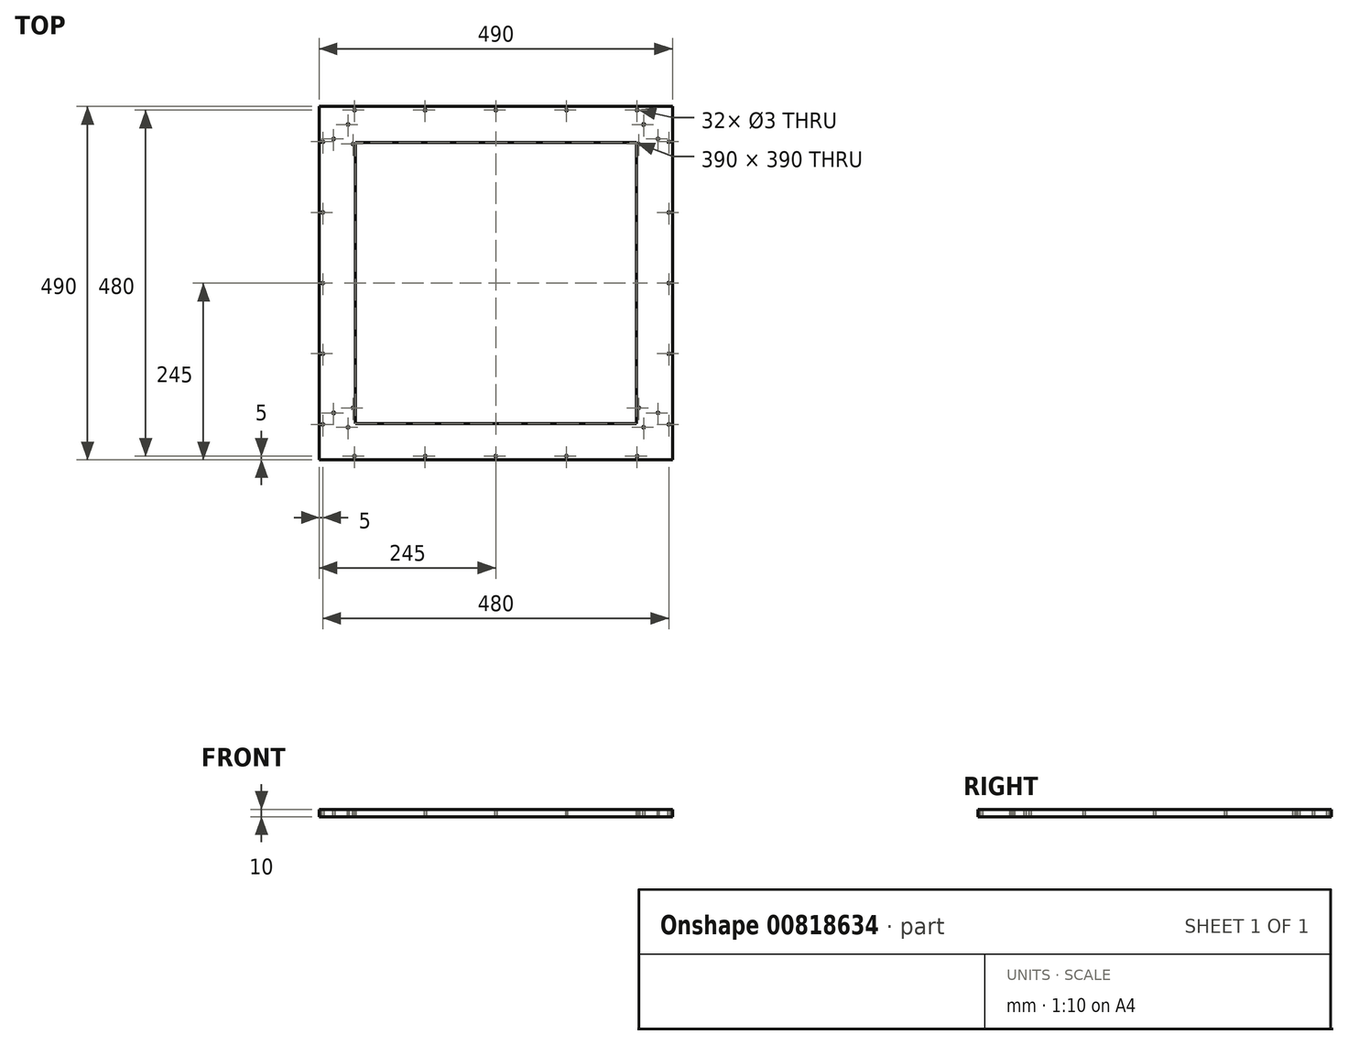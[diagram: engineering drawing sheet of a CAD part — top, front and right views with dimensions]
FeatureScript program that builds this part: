
annotation { "Feature Type Name" : "Feature", "Feature Type Description" : "" }
export const myFeature = defineFeature(function(context is Context, id is Id, definition is map)
    precondition{}
    {
        {
            var Q0;
            Q0=qCreatedBy(makeId("Top.planeOp"),FACE);
            var sketch = newSketch(context, id + "F0", { "sketchPlane" : qUnion([Q0])});
            skLineSegment(sketch, "E0.bottom", {"start": v(0, 0) * mm, "end": v(390, 0) * mm});
            skLineSegment(sketch, "E0.top", {"start": v(0, 390) * mm, "end": v(390, 390) * mm});
            skLineSegment(sketch, "E0.left", {"start": v(0, 0) * mm, "end": v(0, 390) * mm});
            skLineSegment(sketch, "E0.right", {"start": v(390, 0) * mm, "end": v(390, 390) * mm});
            skLineSegment(sketch, "E1", {"start": v(0, 0) * mm, "end": v(0, -40) * mm, "construction": true});
            skLineSegment(sketch, "E2", {"start": v(0, -40) * mm, "end": v(-40, -40) * mm, "construction": true});
            skLineSegment(sketch, "E3.bottom", {"start": v(-40, -40) * mm, "end": v(430, -40) * mm});
            skLineSegment(sketch, "E3.top", {"start": v(-40, 430) * mm, "end": v(430, 430) * mm});
            skLineSegment(sketch, "E3.left", {"start": v(-40, -40) * mm, "end": v(-40, 430) * mm});
            skLineSegment(sketch, "E3.right", {"start": v(430, -40) * mm, "end": v(430, 430) * mm});
            skLineSegment(sketch, "E4", {"start": v(-40, 430) * mm, "end": v(-10, 430) * mm});
            skLineSegment(sketch, "E5", {"start": v(-10, 430) * mm, "end": v(-10, 395) * mm});
            skLineSegment(sketch, "E6", {"start": v(-10, 395) * mm, "end": v(-10, 415) * mm});
            skLineSegment(sketch, "E7", {"start": v(-10, 395) * mm, "end": v(-30, 395) * mm});
            skCircle(sketch, "E8", {"center": v(-30, 395) * mm, "radius": 1.5 * mm});
            skCircle(sketch, "E9", {"center": v(-10, 415) * mm, "radius": 1.5 * mm});
            skLineSegment(sketch, "E10.bottom", {"start": v(-10, 395) * mm, "end": v(-3, 395) * mm, "construction": true});
            skLineSegment(sketch, "E10.top", {"start": v(-10, 388) * mm, "end": v(-3, 388) * mm, "construction": true});
            skLineSegment(sketch, "E10.left", {"start": v(-10, 395) * mm, "end": v(-10, 388) * mm, "construction": true});
            skLineSegment(sketch, "E10.right", {"start": v(-3, 395) * mm, "end": v(-3, 388) * mm, "construction": true});
            skCircle(sketch, "E11", {"center": v(-3, 388) * mm, "radius": 1.5 * mm});
            skLineSegment(sketch, "E12", {"start": v(430, 430) * mm, "end": v(400, 430) * mm});
            skLineSegment(sketch, "E13", {"start": v(400, 430) * mm, "end": v(400, 395) * mm});
            skLineSegment(sketch, "E14", {"start": v(400, 395) * mm, "end": v(400, 415) * mm});
            skLineSegment(sketch, "E15", {"start": v(400, 395) * mm, "end": v(420, 395) * mm});
            skLineSegment(sketch, "E16.bottom", {"start": v(400, 395) * mm, "end": v(393, 395) * mm, "construction": true});
            skLineSegment(sketch, "E16.top", {"start": v(400, 388) * mm, "end": v(393, 388) * mm, "construction": true});
            skLineSegment(sketch, "E16.left", {"start": v(400, 395) * mm, "end": v(400, 388) * mm, "construction": true});
            skLineSegment(sketch, "E16.right", {"start": v(393, 395) * mm, "end": v(393, 388) * mm, "construction": true});
            skCircle(sketch, "E17", {"center": v(393, 388) * mm, "radius": 1.5 * mm});
            skLineSegment(sketch, "E18", {"start": v(-40, -40) * mm, "end": v(-10, -40) * mm});
            skLineSegment(sketch, "E19", {"start": v(-10, -40) * mm, "end": v(-10, 15) * mm});
            skLineSegment(sketch, "E20", {"start": v(-10, 15) * mm, "end": v(-10, -5) * mm});
            skLineSegment(sketch, "E21", {"start": v(-10, 15) * mm, "end": v(-30, 15) * mm});
            skCircle(sketch, "E22", {"center": v(420, 395) * mm, "radius": 1.5 * mm});
            skCircle(sketch, "E23", {"center": v(400, 415) * mm, "radius": 1.5 * mm});
            skCircle(sketch, "E24", {"center": v(-30, 15) * mm, "radius": 1.5 * mm});
            skCircle(sketch, "E25", {"center": v(-10, -5) * mm, "radius": 1.5 * mm});
            skLineSegment(sketch, "E26.bottom", {"start": v(-10, 15) * mm, "end": v(-3, 15) * mm, "construction": true});
            skLineSegment(sketch, "E26.top", {"start": v(-10, 22) * mm, "end": v(-3, 22) * mm, "construction": true});
            skLineSegment(sketch, "E26.left", {"start": v(-10, 15) * mm, "end": v(-10, 22) * mm, "construction": true});
            skLineSegment(sketch, "E26.right", {"start": v(-3, 15) * mm, "end": v(-3, 22) * mm, "construction": true});
            skCircle(sketch, "E27", {"center": v(-3, 22) * mm, "radius": 1.5 * mm});
            skLineSegment(sketch, "E28", {"start": v(430, -40) * mm, "end": v(400, -40) * mm});
            skLineSegment(sketch, "E29", {"start": v(400, -40) * mm, "end": v(400, 15) * mm});
            skLineSegment(sketch, "E30", {"start": v(400, 15) * mm, "end": v(400, -5) * mm});
            skLineSegment(sketch, "E31", {"start": v(400, 15) * mm, "end": v(420, 15) * mm});
            skLineSegment(sketch, "E32.bottom", {"start": v(400, 15) * mm, "end": v(393, 15) * mm, "construction": true});
            skLineSegment(sketch, "E32.top", {"start": v(400, 22) * mm, "end": v(393, 22) * mm, "construction": true});
            skLineSegment(sketch, "E32.left", {"start": v(400, 15) * mm, "end": v(400, 22) * mm, "construction": true});
            skLineSegment(sketch, "E32.right", {"start": v(393, 15) * mm, "end": v(393, 22) * mm, "construction": true});
            skCircle(sketch, "E33", {"center": v(393, 22) * mm, "radius": 1.5 * mm});
            skCircle(sketch, "E34", {"center": v(420, 15) * mm, "radius": 1.5 * mm});
            skCircle(sketch, "E35", {"center": v(400, -5) * mm, "radius": 1.5 * mm});
            skLineSegment(sketch, "E36.bottom", {"start": v(-40, -40) * mm, "end": v(-50, -40) * mm});
            skLineSegment(sketch, "E36.top", {"start": v(-40, -50) * mm, "end": v(-50, -50) * mm});
            skLineSegment(sketch, "E36.left", {"start": v(-40, -40) * mm, "end": v(-40, -50) * mm});
            skLineSegment(sketch, "E36.right", {"start": v(-50, -40) * mm, "end": v(-50, -50) * mm});
            skLineSegment(sketch, "E37.bottom", {"start": v(-50, -50) * mm, "end": v(440, -50) * mm});
            skLineSegment(sketch, "E37.top", {"start": v(-50, 440) * mm, "end": v(440, 440) * mm});
            skLineSegment(sketch, "E37.left", {"start": v(-50, -50) * mm, "end": v(-50, 440) * mm});
            skLineSegment(sketch, "E37.right", {"start": v(440, -50) * mm, "end": v(440, 440) * mm});
            skLineSegment(sketch, "E38", {"start": v(-50, -45) * mm, "end": v(-1, -45) * mm, "construction": true});
            skLineSegment(sketch, "E39", {"start": v(-1, -45) * mm, "end": v(97, -45) * mm, "construction": true});
            skLineSegment(sketch, "E40", {"start": v(97, -45) * mm, "end": v(195, -45) * mm, "construction": true});
            skLineSegment(sketch, "E41", {"start": v(195, -45) * mm, "end": v(293, -45) * mm, "construction": true});
            skLineSegment(sketch, "E42", {"start": v(293, -45) * mm, "end": v(391, -45) * mm, "construction": true});
            skLineSegment(sketch, "E43", {"start": v(-45, -50) * mm, "end": v(-45, -1) * mm, "construction": true});
            skLineSegment(sketch, "E44", {"start": v(-45, -1) * mm, "end": v(-45, 97) * mm, "construction": true});
            skLineSegment(sketch, "E45", {"start": v(-45, 97) * mm, "end": v(-45, 195) * mm, "construction": true});
            skLineSegment(sketch, "E46", {"start": v(-45, 195) * mm, "end": v(-45, 293) * mm, "construction": true});
            skLineSegment(sketch, "E47", {"start": v(-45, 293) * mm, "end": v(-45, 391) * mm, "construction": true});
            skLineSegment(sketch, "E48", {"start": v(430, 430) * mm, "end": v(440, 430) * mm});
            skLineSegment(sketch, "E49", {"start": v(430, 430) * mm, "end": v(430, 440) * mm});
            skLineSegment(sketch, "E50", {"start": v(435, 430) * mm, "end": v(435, 391) * mm, "construction": true});
            skLineSegment(sketch, "E51", {"start": v(435, 391) * mm, "end": v(435, 293) * mm, "construction": true});
            skLineSegment(sketch, "E52", {"start": v(435, 293) * mm, "end": v(435, 195) * mm, "construction": true});
            skLineSegment(sketch, "E53", {"start": v(435, 195) * mm, "end": v(435, 97) * mm, "construction": true});
            skLineSegment(sketch, "E54", {"start": v(435, 97) * mm, "end": v(435, -1) * mm, "construction": true});
            skCircle(sketch, "E55", {"center": v(435, 391) * mm, "radius": 1.5 * mm});
            skCircle(sketch, "E56", {"center": v(435, 293) * mm, "radius": 1.5 * mm});
            skCircle(sketch, "E57", {"center": v(435, 195) * mm, "radius": 1.5 * mm});
            skCircle(sketch, "E58", {"center": v(435, 97) * mm, "radius": 1.5 * mm});
            skCircle(sketch, "E59", {"center": v(435, -1) * mm, "radius": 1.5 * mm});
            skCircle(sketch, "E60", {"center": v(391, -45) * mm, "radius": 1.5 * mm});
            skCircle(sketch, "E61", {"center": v(293, -45) * mm, "radius": 1.5 * mm});
            skCircle(sketch, "E62", {"center": v(195, -45) * mm, "radius": 1.5 * mm});
            skCircle(sketch, "E63", {"center": v(97, -45) * mm, "radius": 1.5 * mm});
            skCircle(sketch, "E64", {"center": v(-1, -45) * mm, "radius": 1.5 * mm});
            skCircle(sketch, "E65", {"center": v(-45, -1) * mm, "radius": 1.5 * mm});
            skCircle(sketch, "E66", {"center": v(-45, 97) * mm, "radius": 1.5 * mm});
            skCircle(sketch, "E67", {"center": v(-45, 195) * mm, "radius": 1.5 * mm});
            skCircle(sketch, "E68", {"center": v(-45, 293) * mm, "radius": 1.5 * mm});
            skCircle(sketch, "E69", {"center": v(-45, 391) * mm, "radius": 1.5 * mm});
            skLineSegment(sketch, "E70", {"start": v(430, 440) * mm, "end": v(430, 435) * mm});
            skLineSegment(sketch, "E71", {"start": v(430, 435) * mm, "end": v(391, 435) * mm, "construction": true});
            skLineSegment(sketch, "E72", {"start": v(391, 435) * mm, "end": v(293, 435) * mm, "construction": true});
            skLineSegment(sketch, "E73", {"start": v(293, 435) * mm, "end": v(195, 435) * mm, "construction": true});
            skLineSegment(sketch, "E74", {"start": v(195, 435) * mm, "end": v(97, 435) * mm, "construction": true});
            skLineSegment(sketch, "E75", {"start": v(97, 435) * mm, "end": v(-1, 435) * mm, "construction": true});
            skCircle(sketch, "E76", {"center": v(391, 435) * mm, "radius": 1.5 * mm});
            skCircle(sketch, "E77", {"center": v(293, 435) * mm, "radius": 1.5 * mm});
            skCircle(sketch, "E78", {"center": v(195, 435) * mm, "radius": 1.5 * mm});
            skCircle(sketch, "E79", {"center": v(97, 435) * mm, "radius": 1.5 * mm});
            skCircle(sketch, "E80", {"center": v(-1, 435) * mm, "radius": 1.5 * mm});
            skSolve(sketch);
        }
        {
            var Q0;
            Q0=makeQuery(id+"F0.imprint","IMPRINT",FACE,{"disambiguationData":[TD([[makeQuery(id+"F0.imprint","IMPRINT",EDGE,{"derivedFrom":sQuery(id+"F0.wireOp",EDGE,"E3.bottom")}),-1.0]])]});
            var Q1;
            Q1=makeQuery(id+"F0.imprint","IMPRINT",FACE,{"disambiguationData":[TD([[makeQuery(id+"F0.imprint","IMPRINT",EDGE,{"derivedFrom":sQuery(id+"F0.wireOp",EDGE,"E0.bottom")}),-1.0]])]});
            var Q2;
            {var subQ0=sQuery(id+"F0.wireOp",EDGE,"E36.bottom");Q2=makeQuery(id+"F0.imprint","IMPRINT",FACE,{"disambiguationData":[TD([[makeQuery(id+"F0.imprint","IMPRINT",EDGE,{"derivedFrom":subQ0}),1.0]])]});}
            var Q3;
            Q3=makeQuery(id+"F0.imprint","IMPRINT",FACE,{"disambiguationData":[TD([[makeQuery(id+"F0.imprint","IMPRINT",EDGE,{"derivedFrom":sQuery(id+"F0.wireOp",EDGE,"E3.top")}),1.0]])]});
            var Q4;
            {var subQ4=sQuery(id+"F0.wireOp",EDGE,"E48");Q4=makeQuery(id+"F0.imprint","IMPRINT",FACE,{"disambiguationData":[TD([[makeQuery(id+"F0.imprint","IMPRINT",EDGE,{"derivedFrom":subQ4}),1.0]])]});}
            extrude(context, id + "F1", {"entities" : qUnion([Q0, Q1, Q2, Q3, Q4]), "depth" : 10 * mm, "offsetDistance" : 25 * mm});
        }
    });
